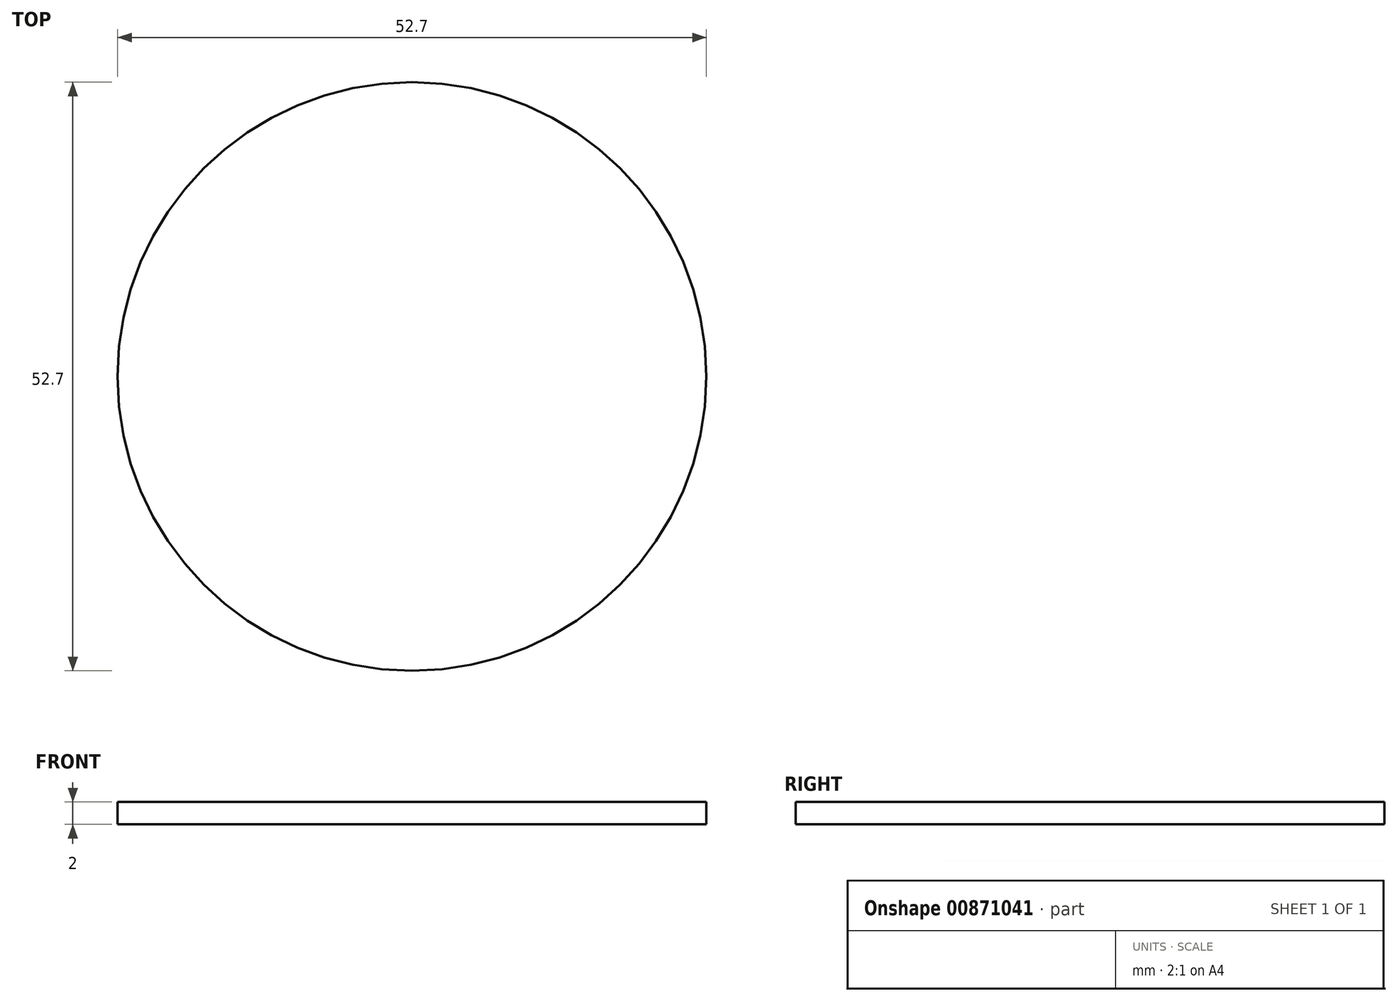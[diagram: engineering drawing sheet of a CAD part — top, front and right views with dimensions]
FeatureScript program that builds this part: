
annotation { "Feature Type Name" : "Feature", "Feature Type Description" : "" }
export const myFeature = defineFeature(function(context is Context, id is Id, definition is map)
    precondition{}
    {
        {
            var Q0;
            Q0=qCreatedBy(makeId("Top.planeOp"),FACE);
            var sketch = newSketch(context, id + "F0", { "sketchPlane" : qUnion([Q0])});
            skCircle(sketch, "E0", {"center": v(0, 0) * mm, "radius": 26.35 * mm});
            skSolve(sketch);
        }
        {
            var Q0;
            Q0 = qSketchRegion(id + "F0", true);
            extrude(context, id + "F1", {"entities" : qUnion([Q0]), "depth" : 2 * mm, "offsetDistance" : 25.4 * mm});
        }
    });
